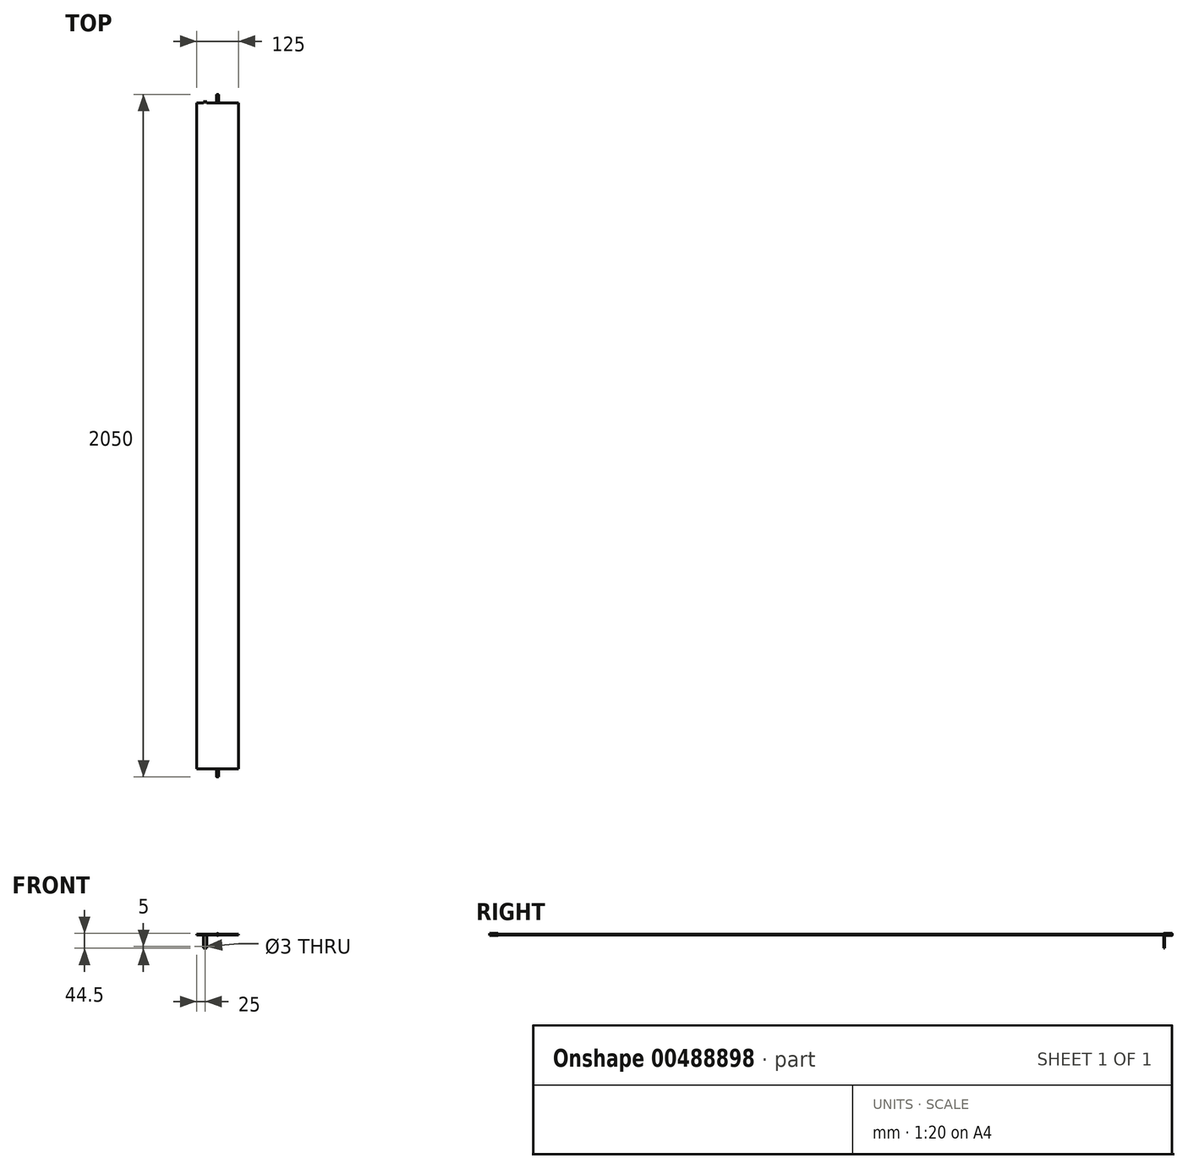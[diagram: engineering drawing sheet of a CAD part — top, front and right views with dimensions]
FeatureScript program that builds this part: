
annotation { "Feature Type Name" : "Feature", "Feature Type Description" : "" }
export const myFeature = defineFeature(function(context is Context, id is Id, definition is map)
    precondition{}
    {
        {
            var Q0;
            Q0=qCreatedBy(makeId("Top.planeOp"),FACE);
            var sketch = newSketch(context, id + "F0", { "sketchPlane" : qUnion([Q0])});
            skLineSegment(sketch, "E0.left", {"start": v(-34.4, 1855.8) * mm, "end": v(-34.4, -144.2) * mm});
            skLineSegment(sketch, "E0.right", {"start": v(90.6, 1855.8) * mm, "end": v(90.6, -144.2) * mm});
            skLineSegment(sketch, "E1", {"start": v(-34.4, 1855.8) * mm, "end": v(25.6, 1855.8) * mm});
            skLineSegment(sketch, "E2", {"start": v(25.6, 1855.8) * mm, "end": v(25.6, 1875.8) * mm});
            skLineSegment(sketch, "E3", {"start": v(25.6, 1875.8) * mm, "end": v(30.6, 1875.8) * mm});
            skLineSegment(sketch, "E4", {"start": v(30.6, 1875.8) * mm, "end": v(30.6, 1855.8) * mm});
            skLineSegment(sketch, "E5", {"start": v(30.6, 1855.8) * mm, "end": v(90.6, 1855.8) * mm});
            skLineSegment(sketch, "E6", {"start": v(-34.4, -144.2) * mm, "end": v(25.6, -144.2) * mm});
            skLineSegment(sketch, "E7", {"start": v(25.6, -144.2) * mm, "end": v(25.6, -164.2) * mm});
            skLineSegment(sketch, "E8", {"start": v(25.6, -164.2) * mm, "end": v(30.6, -164.2) * mm});
            skLineSegment(sketch, "E9", {"start": v(30.6, -164.2) * mm, "end": v(30.6, -144.2) * mm});
            skLineSegment(sketch, "E10", {"start": v(30.6, -144.2) * mm, "end": v(90.6, -144.2) * mm});
            skSolve(sketch);
        }
        {
            var Q0;
            Q0=makeQuery(id+"F0.imprint","IMPRINT",FACE,{"disambiguationData":[TD([[makeQuery(id+"F0.imprint","IMPRINT",EDGE,{"derivedFrom":sQuery(id+"F0.wireOp",EDGE,"E0.bottom")}),-1.0]])]});
            var Q1;
            Q1=makeQuery(id+"F0.imprint","IMPRINT",FACE,{"disambiguationData":[TD([[makeQuery(id+"F0.imprint","IMPRINT",EDGE,{"derivedFrom":sQuery(id+"F0.wireOp",EDGE,"E0.left")}),1.0]])]});
            extrude(context, id + "F1", {"entities" : qUnion([Q0, Q1]), "depth" : 3 * mm});
        }
        {
            var Q0;
            Q0=makeQuery(id+"F1.opExtrude","SWEPT_FACE",FACE,{"disambiguationData":[OSD([sQuery(id+"F0.wireOp",EDGE,"E1")])]});
            var sketch = newSketch(context, id + "F2", { "sketchPlane" : qUnion([Q0])});
            skLineSegment(sketch, "E11.bottom", {"start": v(4.4, 3) * mm, "end": v(14.4, 3) * mm});
            skLineSegment(sketch, "E11.top", {"start": v(4.4, -40) * mm, "end": v(14.4, -40) * mm});
            skLineSegment(sketch, "E11.left", {"start": v(4.4, 3) * mm, "end": v(4.4, -40) * mm});
            skLineSegment(sketch, "E11.right", {"start": v(14.4, 3) * mm, "end": v(14.4, -40) * mm});
            skCircle(sketch, "E12", {"center": v(9.4, -35) * mm, "radius": 1.5 * mm});
            skSolve(sketch);
        }
        {
            var Q0;
            {var subQ0=sQuery(id+"F2.wireOp",EDGE,"E11.bottom");Q0=makeQuery(id+"F2.imprint","IMPRINT",FACE,{"disambiguationData":[TD([[makeQuery(id+"F2.imprint","IMPRINT",EDGE,{"derivedFrom":subQ0}),1.0]])]});}
            var Q1;
            {var subQ1=sQuery(id+"F2.wireOp",EDGE,"E11.top");Q1=makeQuery(id+"F2.imprint","IMPRINT",FACE,{"disambiguationData":[TD([[makeQuery(id+"F2.imprint","IMPRINT",EDGE,{"derivedFrom":subQ1}),1.0]])]});}
            extrude(context, id + "F3", {"entities" : qUnion([Q0, Q1]), "operationType" : NewBodyOperationType.ADD, "depth" : 3 * mm});
        }
        {
            var Q0;
            Q0=makeQuery(id+"F1.opExtrude","SWEPT_FACE",FACE,{"disambiguationData":[OSD([sQuery(id+"F0.wireOp",EDGE,"E10")])]});
            var sketch = newSketch(context, id + "F4", { "sketchPlane" : qUnion([Q0])});
            skCircle(sketch, "E13", {"center": v(28.1, 1.5) * mm, "radius": 3 * mm});
            skSolve(sketch);
        }
        {
            var Q0;
            {var subQ1=sQuery(id+"F0.wireOp",EDGE,"E10");var subQ6=makeQuery(id+"F1.opExtrude","SWEPT_EDGE",EDGE,{"disambiguationData":[OSD([sQuery(id+"F0.wireOp",EDGE,"E9"),subQ1])]});Q0=makeQuery(id+"F4.imprint","IMPRINT",FACE,{"disambiguationData":[TD([[makeQuery(id+"F4.imprint","IMPRINT",EDGE,{"derivedFrom":subQ6}),-1.0]])]});}
            var Q1;
            {var subQ1=sQuery(id+"F0.wireOp",EDGE,"E10");var subQ6=makeQuery(id+"F1.opExtrude","SWEPT_EDGE",EDGE,{"disambiguationData":[OSD([sQuery(id+"F0.wireOp",EDGE,"E9"),subQ1])]});Q1=makeQuery(id+"F4.imprint","IMPRINT",FACE,{"disambiguationData":[TD([[makeQuery(id+"F4.imprint","IMPRINT",EDGE,{"derivedFrom":subQ6}),1.0]])]});}
            extrude(context, id + "F5", {"entities" : qUnion([Q0, Q1]), "operationType" : NewBodyOperationType.ADD, "depth" : 25 * mm});
        }
        {
            var Q0;
            Q0=makeQuery(id+"F1.opExtrude","SWEPT_FACE",FACE,{"disambiguationData":[OSD([sQuery(id+"F0.wireOp",EDGE,"E5")])]});
            var sketch = newSketch(context, id + "F6", { "sketchPlane" : qUnion([Q0])});
            skCircle(sketch, "E14", {"center": v(-28.1, 1.5) * mm, "radius": 3 * mm});
            skSolve(sketch);
        }
        {
            var Q0;
            {var subQ1=sQuery(id+"F0.wireOp",EDGE,"E5");var subQ6=makeQuery(id+"F1.opExtrude","SWEPT_EDGE",EDGE,{"disambiguationData":[OSD([sQuery(id+"F0.wireOp",EDGE,"E4"),subQ1])]});Q0=makeQuery(id+"F6.imprint","IMPRINT",FACE,{"disambiguationData":[TD([[makeQuery(id+"F6.imprint","IMPRINT",EDGE,{"derivedFrom":subQ6}),1.0]])]});}
            var Q1;
            {var subQ1=sQuery(id+"F0.wireOp",EDGE,"E5");var subQ6=makeQuery(id+"F1.opExtrude","SWEPT_EDGE",EDGE,{"disambiguationData":[OSD([sQuery(id+"F0.wireOp",EDGE,"E4"),subQ1])]});Q1=makeQuery(id+"F6.imprint","IMPRINT",FACE,{"disambiguationData":[TD([[makeQuery(id+"F6.imprint","IMPRINT",EDGE,{"derivedFrom":subQ6}),-1.0]])]});}
            extrude(context, id + "F7", {"entities" : qUnion([Q0, Q1]), "operationType" : NewBodyOperationType.ADD, "depth" : 25 * mm});
        }
    });
